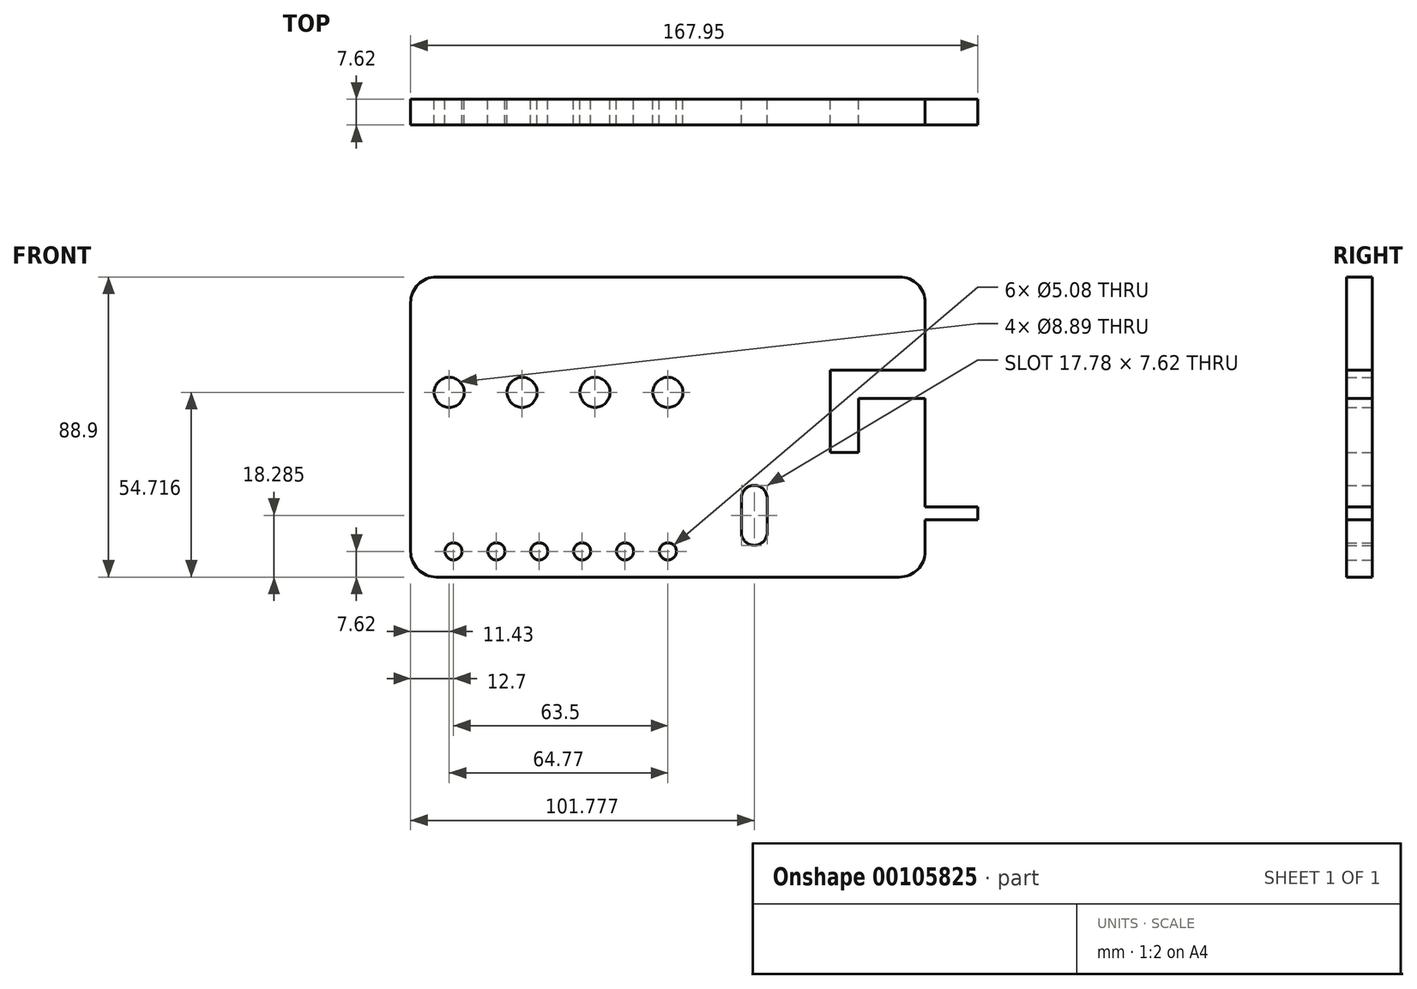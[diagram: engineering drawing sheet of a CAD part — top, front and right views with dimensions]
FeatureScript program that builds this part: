
annotation { "Feature Type Name" : "Feature", "Feature Type Description" : "" }
export const myFeature = defineFeature(function(context is Context, id is Id, definition is map)
    precondition{}
    {
        {
            var Q0;
            Q0=qCreatedBy(makeId("Front.planeOp"),FACE);
            var sketch = newSketch(context, id + "F0", { "sketchPlane" : qUnion([Q0])});
            skLineSegment(sketch, "E0.bottom", {"start": v(68.58, 44.45) * mm, "end": v(-68.58, 44.45) * mm});
            skLineSegment(sketch, "E0.top", {"start": v(68.58, -44.45) * mm, "end": v(-68.58, -44.45) * mm});
            skLineSegment(sketch, "E0.left", {"start": v(76.2, 36.83) * mm, "end": v(76.2, -36.83) * mm});
            skLineSegment(sketch, "E0.right", {"start": v(-76.2, 36.83) * mm, "end": v(-76.2, -36.83) * mm});
            skPoint(sketch, "E0.middle", {"position": v(0, 0) * mm});
            skPoint(sketch, "E1.visualSharp", {"position": v(-76.2, 44.45) * mm});
            skArc(sketch, "E1.filletArc", {"start": v(-68.58, 44.45) * mm, "mid": v(-73.97, 42.22) * mm, "end": v(-76.2, 36.83) * mm});
            skPoint(sketch, "E2.visualSharp", {"position": v(-76.2, -44.45) * mm});
            skArc(sketch, "E2.filletArc", {"start": v(-76.2, -36.83) * mm, "mid": v(-73.97, -42.22) * mm, "end": v(-68.58, -44.45) * mm});
            skPoint(sketch, "E3.visualSharp", {"position": v(76.2, -44.45) * mm});
            skArc(sketch, "E3.filletArc", {"start": v(68.58, -44.45) * mm, "mid": v(73.97, -42.22) * mm, "end": v(76.2, -36.83) * mm});
            skPoint(sketch, "E4.visualSharp", {"position": v(76.2, 44.45) * mm});
            skArc(sketch, "E4.filletArc", {"start": v(76.2, 36.83) * mm, "mid": v(73.97, 42.22) * mm, "end": v(68.58, 44.45) * mm});
            skLineSegment(sketch, "E5", {"start": v(-76.2, -36.83) * mm, "end": v(0, -36.83) * mm});
            skCircle(sketch, "E6", {"center": v(0, -36.83) * mm, "radius": 2.54 * mm});
            skCircle(sketch, "E7", {"center": v(-12.7, -36.83) * mm, "radius": 2.54 * mm});
            skCircle(sketch, "E8", {"center": v(-25.4, -36.83) * mm, "radius": 2.54 * mm});
            skCircle(sketch, "E9", {"center": v(-38.1, -36.83) * mm, "radius": 2.54 * mm});
            skCircle(sketch, "E10", {"center": v(-50.8, -36.83) * mm, "radius": 2.54 * mm});
            skCircle(sketch, "E11", {"center": v(-63.5, -36.83) * mm, "radius": 2.54 * mm});
            skLineSegment(sketch, "E12", {"start": v(-76.2, 10.27) * mm, "end": v(14.05, 10.27) * mm});
            skCircle(sketch, "E13", {"center": v(-64.77, 10.27) * mm, "radius": 4.45 * mm});
            skCircle(sketch, "E14", {"center": v(-43.18, 10.27) * mm, "radius": 4.45 * mm});
            skCircle(sketch, "E15", {"center": v(-21.59, 10.27) * mm, "radius": 4.45 * mm});
            skCircle(sketch, "E16", {"center": v(0, 10.27) * mm, "radius": 4.45 * mm});
            skLineSegment(sketch, "E17.bottom", {"start": v(21.77, -31.25) * mm, "end": v(29.39, -31.25) * mm});
            skLineSegment(sketch, "E17.top", {"start": v(21.77, -21.09) * mm, "end": v(29.39, -21.09) * mm});
            skLineSegment(sketch, "E17.left", {"start": v(21.77, -31.25) * mm, "end": v(21.77, -21.09) * mm});
            skLineSegment(sketch, "E17.right", {"start": v(29.39, -31.25) * mm, "end": v(29.39, -21.09) * mm});
            skArc(sketch, "E18", {"start": v(29.39, -21.09) * mm, "mid": v(25.58, -17.28) * mm, "end": v(21.77, -21.09) * mm});
            skArc(sketch, "E19", {"start": v(21.77, -31.25) * mm, "mid": v(25.58, -35.06) * mm, "end": v(29.39, -31.25) * mm});
            skLineSegment(sketch, "E20.bottom", {"start": v(76.2, 16.87) * mm, "end": v(48.08, 16.87) * mm});
            skLineSegment(sketch, "E20.top", {"start": v(76.2, 8.49) * mm, "end": v(48.08, 8.49) * mm});
            skLineSegment(sketch, "E20.left", {"start": v(76.2, 16.87) * mm, "end": v(76.2, 8.49) * mm});
            skLineSegment(sketch, "E20.right", {"start": v(48.08, 16.87) * mm, "end": v(48.08, 8.49) * mm});
            skLineSegment(sketch, "E21.bottom", {"start": v(48.08, 16.87) * mm, "end": v(56.46, 16.87) * mm});
            skLineSegment(sketch, "E21.top", {"start": v(48.08, -7.6) * mm, "end": v(56.46, -7.6) * mm});
            skLineSegment(sketch, "E21.left", {"start": v(48.08, 16.87) * mm, "end": v(48.08, -7.6) * mm});
            skLineSegment(sketch, "E21.right", {"start": v(56.46, 16.87) * mm, "end": v(56.46, -7.6) * mm});
            skLineSegment(sketch, "E22.bottom", {"start": v(76.2, -27.43) * mm, "end": v(91.75, -27.43) * mm});
            skLineSegment(sketch, "E22.top", {"start": v(76.2, -23.7) * mm, "end": v(91.75, -23.7) * mm});
            skLineSegment(sketch, "E22.left", {"start": v(76.2, -27.43) * mm, "end": v(76.2, -23.7) * mm});
            skLineSegment(sketch, "E22.right", {"start": v(91.75, -27.43) * mm, "end": v(91.75, -23.7) * mm});
            skLineSegment(sketch, "E23.left", {"start": v(21, 6.76) * mm, "end": v(21, 16.92) * mm});
            skLineSegment(sketch, "E23.right", {"start": v(28.62, 6.76) * mm, "end": v(28.62, 16.92) * mm});
            skArc(sketch, "E24", {"start": v(28.62, 16.78) * mm, "mid": v(24.81, 20.73) * mm, "end": v(21, 16.78) * mm});
            skArc(sketch, "E25", {"start": v(21, 6.62) * mm, "mid": v(24.81, 2.95) * mm, "end": v(28.62, 6.62) * mm});
            skSolve(sketch);
        }
        {
            var Q0;
            Q0=makeQuery(id+"F0.imprint","IMPRINT",FACE,{"disambiguationData":[TD([[makeQuery(id+"F0.imprint","IMPRINT",EDGE,{"derivedFrom":sQuery(id+"F0.wireOp",EDGE,"E0.bottom")}),1.0]])]});
            var Q1;
            Q1=makeQuery(id+"F0.imprint","IMPRINT",FACE,{"disambiguationData":[TD([[makeQuery(id+"F0.imprint","IMPRINT",EDGE,{"derivedFrom":sQuery(id+"F0.wireOp",EDGE,"E22.bottom")}),1.0]])]});
            extrude(context, id + "F1", {"entities" : qUnion([Q0, Q1]), "depth" : 7.62 * mm});
        }
    });
